FCSTD DOCUMENT  (FreeCAD 0.21R33771 (Git))
Label: EngineMount_UQM_SF_v2
License: Creative Commons Attribution-ShareAlike 4.0
LicenseURL: https://creativecommons.org/licenses/by-sa/4.0/
objects: PartDesign::CoordinateSystem×3, App::DocumentObjectGroup×3, PartDesign::Line×3, App::Link×3, Sketcher::SketchObject×2, PartDesign::Plane×2, App::Part×2, App::FeaturePython×1, PartDesign::Point×1, PartDesign::Body×1
note: 12 computed .brp shape members not serialized (recipe doc carries the construction recipe); baked Part::Feature solids carry a one-line shape summary decoded from their .brp
EXTERNAL_REF file=FacePlate_Motor_MC_v2.FCStd obj=Body_MotorFace
EXTERNAL_REF file=FacePlate_Motor_MC_v2.FCStd obj=MMFP_Tabs_CtrlMnt
EXTERNAL_REF file=FacePlate_TX_v2.FCStd obj=TXFP_SpacerSide
EXTERNAL_REF file=FacePlate_TX_v2.FCStd obj=TXFP
EXTERNAL_REF file=SpacerFlange_v2.FCStd obj=TabCenterAxis
EXTERNAL_REF file=SpacerFlange_v2.FCStd obj=TabFlange

FEATURE [PartDesign::CoordinateSystem] LCS_Origin
  AttacherType = Attacher::AttachEngine3D
  MapMode = 2
  Support = -> [X_Axis]
FEATURE [App::DocumentObjectGroup] Constraints
FEATURE [App::FeaturePython] Variables  # WARN: FeaturePython — macro-defined, semantics opaque (R4)
  Type = App::PropertyContainer
FEATURE [App::DocumentObjectGroup] Configurations
FEATURE [Sketcher::SketchObject] MotorFaceBase
  FullyConstrained = true
  MapMode = 5
  Support = -> [XY_Plane]
  expr: Constraints[1] = 16 in
  sketch-geometry (17):
    g0: Circle CenterX=0 CenterY=0 CenterZ=0 NormalX=0 NormalY=0 NormalZ=1 AngleXU=0 Radius=203.2
    g1: LineSegment StartX=-117.333 StartY=48.6008 StartZ=0 EndX=-117.333 EndY=-48.6008 EndZ=0
    g2: LineSegment StartX=-117.333 StartY=-48.6008 StartZ=0 EndX=-48.6008 EndY=-117.333 EndZ=0
    g3: LineSegment StartX=-48.6008 StartY=-117.333 StartZ=0 EndX=48.6008 EndY=-117.333 EndZ=0
    g4: LineSegment StartX=48.6008 StartY=-117.333 StartZ=0 EndX=117.333 EndY=-48.6008 EndZ=0
    g5: LineSegment StartX=117.333 StartY=-48.6008 StartZ=0 EndX=117.333 EndY=48.6008 EndZ=0
    g6: LineSegment StartX=117.333 StartY=48.6008 StartZ=0 EndX=48.6008 EndY=117.333 EndZ=0
    g7: LineSegment StartX=48.6008 StartY=117.333 StartZ=0 EndX=-48.6008 EndY=117.333 EndZ=0
    g8: LineSegment StartX=-48.6008 StartY=117.333 StartZ=0 EndX=-117.333 EndY=48.6008 EndZ=0
    g9: Circle CenterX=0 CenterY=0 CenterZ=0 NormalX=0 NormalY=0 NormalZ=1 AngleXU=0 Radius=127
    g10: LineSegment StartX=-152 StartY=0 StartZ=0 EndX=-152 EndY=17 EndZ=0
    g11: LineSegment StartX=-152 StartY=0 StartZ=0 EndX=-152 EndY=-17 EndZ=0
    g12: LineSegment StartX=-150.25 StartY=12 StartZ=0 EndX=-150.25 EndY=22 EndZ=0
    g13: LineSegment StartX=-150.25 StartY=22 StartZ=0 EndX=-153.75 EndY=22 EndZ=0
    g14: LineSegment StartX=-153.75 StartY=22 StartZ=0 EndX=-153.75 EndY=12 EndZ=0
    g15: LineSegment StartX=-153.75 StartY=12 StartZ=0 EndX=-150.25 EndY=12 EndZ=0
    g16: GeomPoint X=-152 Y=17 Z=0
  constraints (41):
    c: Coincident(g0,g-1)
    c: Diameter(g0) = 406.4
    c: Coincident(g1,g2)
    c: Coincident(g2,g3)
    c: Coincident(g3,g4)
    c: Coincident(g4,g5)
    c: Coincident(g5,g6)
    c: Coincident(g6,g7)
    c: Coincident(g7,g8)
    c: Coincident(g8,g1)
    c: Equal(g1, g2-g8) x7
    c: PointOnObject(g1,g9)
    c: PointOnObject(g2,g9)
    c: PointOnObject(g3,g9)
    c: PointOnObject(g4,g9)
    c: PointOnObject(g6,g9)
    c: PointOnObject(g7,g9)
    c: PointOnObject(g8,g9)
    c: Coincident(g9,g0)
    c: Vertical(g1)
    c: Diameter(g9) = 254
    c: PointOnObject(g5,g9)
    c: PointOnObject(g10,g-1)
    c: Vertical(g10)
    c: Coincident(g11,g10)
    c: Vertical(g11)
    c: Equal(g10,g11)
    c: DistanceY(g10,g10) = 17
    c: DistanceX(g10,g0) = 152
    c: Coincident(g12,g13)
    c: Coincident(g13,g14)
    c: Coincident(g14,g15)
    c: Coincident(g15,g12)
    c: Horizontal(g13)
    c: Horizontal(g15)
    c: Vertical(g12)
    c: Vertical(g14)
    c: Symmetric(g13,g12,g16)
    c: Coincident(g16,g10)
    c: DistanceY(g14,g14) = 10
    c: DistanceX(g13,g13) = 3.5
FEATURE [PartDesign::Line] Motor_FirstBolt
  AttacherType = Attacher::AttachEngineLine
  Length = 200
  MapMode = 46
  Placement = pos=(-117.333,48.6008,0) rot=(0,0,1;3.14159rad)
  ResizeMode = 1
  Support = -> [MotorFaceBase,XY_Plane]
FEATURE [PartDesign::Plane] MotorFace
  Length = 100
  MapMode = 5
  ResizeMode = 1
  Support = -> [XY_Plane]
  Width = 100
FEATURE [PartDesign::Line] FirstTabSlot
  AttacherType = Attacher::AttachEngineLine
  Length = 200
  MapMode = 46
  Placement = pos=(-152,17,0) rot=(0,0,1;3.14159rad)
  ResizeMode = 1
  Support = -> [MotorFaceBase,XY_Plane]
FEATURE [App::Link] MMFP_Tabs_CtrlMnt
  AttachedBy = #Body_MotorFace
  AttachedTo = Parent Assembly#MotorFace
  AttachmentOffset = pos=(0,0,0) rot=(-1,0,0;3.14159rad)
  LinkPlacement = pos=(0,0,0) rot=(-1,0,0;1.5708rad)
  LinkedObject = -> <external FacePlate_Motor_MC_v2.FCStd>#MMFP_Tabs_CtrlMnt
  Placement = pos=(0,0,0) rot=(-1,0,0;1.5708rad)
  SolverId = Asm4EE
  expr: Placement = MotorFace.Placement * AttachmentOffset * FaceFlngILC_MntTabs#Body_MotorFace.Placement ^ -1
FEATURE [Sketcher::SketchObject] MMTX_CrossSection
  FullyConstrained = true
  MapMode = 5
  Placement = pos=(0,0,0) rot=(0.57735,0.57735,0.57735;2.0944rad)
  Support = -> [YZ_Plane]
  expr: .Constraints.SpacerDepth = 38 * 2
  sketch-geometry (2):
    g0: LineSegment StartX=0 StartY=0 StartZ=0 EndX=0 EndY=3.5 EndZ=0
    g1: LineSegment StartX=0 StartY=3.5 StartZ=0 EndX=0 EndY=79.5 EndZ=0
  constraints (6):
    c: Coincident(g0,g-1)
    c: Vertical(g0)
    c: Coincident(g1,g0)
    c: Vertical(g1)
    c: DistanceY(g0,g0) = 3.5  'Thickness'
    c: DistanceY(g1,g1) = 76  'SpacerDepth'
FEATURE [PartDesign::Point] TX_CenterPoint
  AttacherType = Attacher::AttachEnginePoint
  MapMode = 37
  Placement = pos=(-1.77e-14,1.77e-14,79.5) rot=(0,0,1;0rad)
  Support = -> [MMTX_CrossSection]
FEATURE [PartDesign::Plane] TC_Face
  Length = 100
  MapMode = 6
  Placement = pos=(-1.77e-14,1.77e-14,79.5) rot=(0,0,1;3.14159rad)
  ResizeMode = 1
  Support = -> [TX_CenterPoint,XY_Plane]
  Width = 100
FEATURE [App::Link] TXFP
  AttachedBy = #TXFP_SpacerSide
  AttachedTo = Parent Assembly#TC_Face
  AttachmentOffset = pos=(0,0,0) rot=(0,-1,0;3.14159rad)
  LinkPlacement = pos=(-1.77e-14,1.77e-14,79.5) rot=(0,0,1;0rad)
  LinkedObject = -> <external FacePlate_TX_v2.FCStd>#TXFP
  Placement = pos=(-1.77e-14,1.77e-14,79.5) rot=(0,0,1;0rad)
  SolverId = Asm4EE
  expr: Placement = TC_Face.Placement * AttachmentOffset * SF_TY755_TRANS_FACEPLATE#TXFP_SpacerSide.Placement ^ -1
FEATURE [App::Link] TabFlange
  AttachedBy = #TabCenterAxis
  AttachedTo = Parent Assembly#FirstTabSlot
  AttachmentOffset = pos=(0,0,41.5) rot=(0,0,1;1.5708rad)
  LinkPlacement = pos=(-152,0,41.5) rot=(0.57735,0.57735,0.57735;4.18879rad)
  LinkedObject = -> <external SpacerFlange_v2.FCStd>#TabFlange
  Placement = pos=(-152,0,41.5) rot=(0.57735,0.57735,0.57735;4.18879rad)
  SolverId = Asm4EE
  expr: Placement = FirstTabSlot.Placement * AttachmentOffset * SpacerFlange#TabCenterAxis.Placement ^ -1
FEATURE [PartDesign::Line] CenterLine
  AttacherType = Attacher::AttachEngineLine
  Length = 200
  MapMode = 29
  ResizeMode = 1
  Support = -> [Z_Axis]
FEATURE [App::Part] Assembly
  AssemblyType = Part::Link
  Group = -> [LCS_Origin,Constraints,Variables,Configurations,MotorFaceBase,Motor_FirstBolt,MotorFace,FirstTabSlot,MMFP_Tabs_CtrlMnt,MMTX_CrossSection,TX_CenterPoint,TC_Face,TXFP,CenterLine,TabFlange]
  Origin = -> Origin
  Type = Assembly
FEATURE [PartDesign::CoordinateSystem] LCS_Origin001
  AttacherType = Attacher::AttachEngine3D
  MapMode = 2
  Support = -> [X_Axis001]
FEATURE [PartDesign::CoordinateSystem] LCS_Origin002
  AttacherType = Attacher::AttachEngine3D
  MapMode = 2
  Support = -> [X_Axis002]
FEATURE [PartDesign::Body] Body
  Group = -> [LCS_Origin002]
  Origin = -> Origin002
FEATURE [App::Part] TabFlangePattern
  Group = -> [LCS_Origin001,Body]
  Origin = -> Origin001
FEATURE [App::DocumentObjectGroup] Parts
  Group = -> [TabFlangePattern]

RESOLVED EXTERNAL PARTS (link-assembly join: the EXTERNAL_REF files above that resolve inside this repo's crawl, each included once):
---- part FacePlate_Motor_MC_v2.FCStd = doc fcstd_9c76934eff34 ----
FCSTD DOCUMENT  (FreeCAD 0.21R33771 (Git))
Label: FacePlate_Motor_MC_v2
License: Creative Commons Attribution-ShareAlike 4.0
LicenseURL: https://creativecommons.org/licenses/by-sa/4.0/
objects: Sketcher::SketchObject×5, PartDesign::Line×4, PartDesign::Pocket×3, PartDesign::Pad×2, PartDesign::PolarPattern×2, PartDesign::Plane×2, PartDesign::CoordinateSystem×1, PartDesign::Fillet×1, PartDesign::Body×1, App::Part×1
note: 27 computed .brp shape members not serialized (recipe doc carries the construction recipe); baked Part::Feature solids carry a one-line shape summary decoded from their .brp

FEATURE [Sketcher::SketchObject] Sketch
  FullyConstrained = true
  MapMode = 5
  Placement = pos=(0,0,0) rot=(1,0,0;1.5708rad)
  Support = -> [XZ_Plane]
  sketch-geometry (24):
    g0: Circle CenterX=0 CenterY=0 CenterZ=0 NormalX=0 NormalY=0 NormalZ=1 AngleXU=0 Radius=127
    g1: Circle CenterX=-127 CenterY=0 CenterZ=0 NormalX=0 NormalY=0 NormalZ=1 AngleXU=0 Radius=15
    g2: LineSegment StartX=-127 StartY=0 StartZ=0 EndX=-142 EndY=0 EndZ=0
    g3: Circle CenterX=0 CenterY=0 CenterZ=0 NormalX=0 NormalY=0 NormalZ=1 AngleXU=0 Radius=200
    g4: Circle CenterX=0 CenterY=0 CenterZ=0 NormalX=0 NormalY=0 NormalZ=1 AngleXU=0 Radius=100
    g5: LineSegment StartX=-152 StartY=62.9605 StartZ=0 EndX=-152 EndY=-62.9605 EndZ=0
    g6: LineSegment StartX=-152 StartY=-62.9605 StartZ=0 EndX=-62.9605 EndY=-152 EndZ=0
    g7: LineSegment StartX=-62.9605 StartY=-152 StartZ=0 EndX=62.9605 EndY=-152 EndZ=0
    g8: LineSegment StartX=62.9605 StartY=-152 StartZ=0 EndX=152 EndY=-62.9605 EndZ=0
    g9: LineSegment StartX=152 StartY=-62.9605 StartZ=0 EndX=152 EndY=62.9605 EndZ=0
    g10: LineSegment StartX=152 StartY=62.9605 StartZ=0 EndX=62.9605 EndY=152 EndZ=0
    g11: LineSegment StartX=62.9605 StartY=152 StartZ=0 EndX=-62.9605 EndY=152 EndZ=0
    g12: LineSegment StartX=-62.9605 StartY=152 StartZ=0 EndX=-152 EndY=62.9605 EndZ=0
    g13: Circle CenterX=0 CenterY=0 CenterZ=0 NormalX=0 NormalY=0 NormalZ=1 AngleXU=0 Radius=164.524
    g14: LineSegment StartX=-153.75 StartY=22.75 StartZ=0 EndX=-153.75 EndY=33.25 EndZ=0
    g15: LineSegment StartX=-153.75 StartY=33.25 StartZ=0 EndX=-150.25 EndY=33.25 EndZ=0
    g16: LineSegment StartX=-150.25 StartY=33.25 StartZ=0 EndX=-150.25 EndY=22.75 EndZ=0
    g17: LineSegment StartX=-150.25 StartY=22.75 StartZ=0 EndX=-153.75 EndY=22.75 EndZ=0
    g18: GeomPoint X=-152 Y=28 Z=0
    g19: LineSegment StartX=-150.25 StartY=-22.75 StartZ=0 EndX=-150.25 EndY=-33.25 EndZ=0
    g20: LineSegment StartX=-150.25 StartY=-33.25 StartZ=0 EndX=-153.75 EndY=-33.25 EndZ=0
    g21: LineSegment StartX=-153.75 StartY=-33.25 StartZ=0 EndX=-153.75 EndY=-22.75 EndZ=0
    g22: LineSegment StartX=-153.75 StartY=-22.75 StartZ=0 EndX=-150.25 EndY=-22.75 EndZ=0
    g23: GeomPoint X=-152 Y=-28 Z=0
  constraints (60):
    c: Coincident(g0,g-1)
    c: PointOnObject(g1,g0)
    c: Diameter(g1) = 30
    c: Diameter(g0) = 254
    c: PointOnObject(g1,g-1)
    c: Coincident(g2,g1)
    c: PointOnObject(g2,g1)
    c: Horizontal(g2)
    c: Coincident(g3,g0)
    c: Diameter(g3) = 400
    c: Diameter(g4) = 200
    c: Coincident(g4,g3)
    c: Coincident(g5,g6)
    c: Coincident(g6,g7)
    c: Coincident(g7,g8)
    c: Coincident(g8,g9)
    c: Coincident(g9,g10)
    c: Coincident(g10,g11)
    c: Coincident(g11,g12)
    c: Coincident(g12,g5)
    c: Equal(g5, g6-g12) x7
    c: PointOnObject(g5,g13)
    c: PointOnObject(g6,g13)
    c: PointOnObject(g7,g13)
    c: PointOnObject(g8,g13)
    c: PointOnObject(g9,g13)
    c: PointOnObject(g10,g13)
    c: PointOnObject(g11,g13)
    c: PointOnObject(g12,g13)
    c: Coincident(g13,g3)
    c: Vertical(g5)
    c: DistanceX(g5,g2) = 10
    c: Coincident(g14,g15)
    c: Coincident(g15,g16)
    c: Coincident(g16,g17)
    c: Coincident(g17,g14)
    c: Horizontal(g15)
    c: Horizontal(g17)
    c: Vertical(g14)
    c: Vertical(g16)
    c: Symmetric(g15,g14,g18)
    c: PointOnObject(g18,g5)
    c: Coincident(g19,g20)
    c: Coincident(g20,g21)
    c: Coincident(g21,g22)
    c: Coincident(g22,g19)
    c: Horizontal(g20)
    c: Horizontal(g22)
    c: Vertical(g19)
    c: Vertical(g21)
    c: Symmetric(g20,g19,g23)
    c: PointOnObject(g23,g5)
    c: Equal(g14,g21)
    c: Equal(g15,g22)
    c: DistanceX(g15,g15) = 3.5
    c: DistanceY(g14,g14) = 10.5
    c: DistanceY(g3,g14) = 22.75
    c: DistanceY(g19,g3) = 22.75
    c: DistanceY(g3,g18) = 28
    c: DistanceY(g23,g3) = 28
FEATURE [PartDesign::Pad] Pad
  Direction = (0,-1,-2e-16)
  Length = 3
  Length2 = 10
  Placement = pos=(0,0,0) rot=(1,0,0;1.5708rad)
  Profile = -> Sketch
  ReferenceAxis = -> Sketch [N_Axis]
  Type = 0
FEATURE [Sketcher::SketchObject] Sketch001
  FullyConstrained = true
  MapMode = 5
  Placement = pos=(0,0,0) rot=(1,0,0;1.5708rad)
  Support = -> [XZ_Plane]
  expr: Constraints[10] = Sketch.Constraints[10]
  expr: Constraints[2] = Sketch.Constraints[2]
  expr: Constraints[37] = Sketch.Constraints[37]
  expr: Constraints[3] = Sketch.Constraints[3]
  expr: Constraints[61] = Sketch.Constraints[61]
  expr: Constraints[9] = Sketch.Constraints[9]
  sketch-geometry (24):
    g0: Circle CenterX=0 CenterY=0 CenterZ=0 NormalX=0 NormalY=0 NormalZ=1 AngleXU=0 Radius=127
    g1: Circle CenterX=-127 CenterY=0 CenterZ=0 NormalX=0 NormalY=0 NormalZ=1 AngleXU=0 Radius=15
    g2: LineSegment StartX=-127 StartY=0 StartZ=0 EndX=-142 EndY=0 EndZ=0
    g3: Circle CenterX=0 CenterY=0 CenterZ=0 NormalX=0 NormalY=0 NormalZ=1 AngleXU=0 Radius=200
    g4: Circle CenterX=0 CenterY=0 CenterZ=0 NormalX=0 NormalY=0 NormalZ=1 AngleXU=0 Radius=100
    g5: LineSegment StartX=-152 StartY=62.9605 StartZ=0 EndX=-152 EndY=-62.9605 EndZ=0
    g6: LineSegment StartX=-152 StartY=-62.9605 StartZ=0 EndX=-62.9605 EndY=-152 EndZ=0
    g7: LineSegment StartX=-62.9605 StartY=-152 StartZ=0 EndX=62.9605 EndY=-152 EndZ=0
    g8: LineSegment StartX=62.9605 StartY=-152 StartZ=0 EndX=152 EndY=-62.9605 EndZ=0
    g9: LineSegment StartX=152 StartY=-62.9605 StartZ=0 EndX=152 EndY=62.9605 EndZ=0
    g10: LineSegment StartX=152 StartY=62.9605 StartZ=0 EndX=62.9605 EndY=152 EndZ=0
    g11: LineSegment StartX=62.9605 StartY=152 StartZ=0 EndX=-62.9605 EndY=152 EndZ=0
    g12: LineSegment StartX=-62.9605 StartY=152 StartZ=0 EndX=-152 EndY=62.9605 EndZ=0
    g13: Circle CenterX=0 CenterY=0 CenterZ=0 NormalX=0 NormalY=0 NormalZ=1 AngleXU=0 Radius=164.524
    g14: LineSegment StartX=-153.75 StartY=22.75 StartZ=0 EndX=-153.75 EndY=33.25 EndZ=0
    g15: LineSegment StartX=-153.75 StartY=33.25 StartZ=0 EndX=-150.25 EndY=33.25 EndZ=0
    g16: LineSegment StartX=-150.25 StartY=33.25 StartZ=0 EndX=-150.25 EndY=22.75 EndZ=0
    g17: LineSegment StartX=-150.25 StartY=22.75 StartZ=0 EndX=-153.75 EndY=22.75 EndZ=0
    g18: GeomPoint X=-152 Y=28 Z=0
    g19: LineSegment StartX=-150.25 StartY=-22.75 StartZ=0 EndX=-150.25 EndY=-33.25 EndZ=0
    g20: LineSegment StartX=-150.25 StartY=-33.25 StartZ=0 EndX=-153.75 EndY=-33.25 EndZ=0
    g21: LineSegment StartX=-153.75 StartY=-33.25 StartZ=0 EndX=-153.75 EndY=-22.75 EndZ=0
    g22: LineSegment StartX=-153.75 StartY=-22.75 StartZ=0 EndX=-150.25 EndY=-22.75 EndZ=0
    g23: GeomPoint X=-152 Y=-28 Z=0
  constraints (62):
    c: Coincident(g0,g-1)
    c: PointOnObject(g1,g0)
    c: Diameter(g1) = 30
    c: Diameter(g0) = 254
    c: PointOnObject(g1,g-1)
    c: Coincident(g2,g1)
    c: PointOnObject(g2,g1)
    c: Horizontal(g2)
    c: Coincident(g3,g0)
    c: Diameter(g3) = 400
    c: Diameter(g4) = 200
    c: Coincident(g4,g3)
    c: Coincident(g5,g6)
    c: Coincident(g6,g7)
    c: Coincident(g7,g8)
    c: Coincident(g8,g9)
    c: Coincident(g9,g10)
    c: Coincident(g10,g11)
    c: Coincident(g11,g12)
    c: Coincident(g12,g5)
    c: Equal(g5, g6-g12) x7
    c: PointOnObject(g5,g13)
    c: PointOnObject(g6,g13)
    c: PointOnObject(g7,g13)
    c: PointOnObject(g8,g13)
    c: PointOnObject(g9,g13)
    c: PointOnObject(g10,g13)
    c: PointOnObject(g11,g13)
    c: PointOnObject(g12,g13)
    c: Coincident(g13,g3)
    c: Vertical(g5)
    c: DistanceX(g5,g2) = 10
    c: Coincident(g14,g15)
    c: Coincident(g15,g16)
    c: Coincident(g16,g17)
    c: Coincident(g17,g14)
    c: Horizontal(g15)
    c: Horizontal(g17)
    c: Vertical(g14)
    c: Vertical(g16)
    c: Symmetric(g15,g14,g18)
    c: PointOnObject(g18,g5)
    c: Coincident(g19,g20)
    c: Coincident(g20,g21)
    c: Coincident(g21,g22)
    c: Coincident(g22,g19)
    c: Horizontal(g20)
    c: Horizontal(g22)
    c: Vertical(g19)
    c: Vertical(g21)
    c: Symmetric(g20,g19,g23)
    c: PointOnObject(g23,g5)
    c: Equal(g14,g21)
    c: Equal(g15,g22)
    c: DistanceX(g15,g15) = 3.5
    c: DistanceY(g14,g14) = 10.5
    c: DistanceY(g3,g14) = 22.75
    c: DistanceY(g19,g3) = 22.75
    c: DistanceX(g18,g0) = 152
    c: DistanceY(g0,g5) = 62.9605
    c: DistanceY(g0,g18) = 28
    c: DistanceY(g23,g0) = 28
FEATURE [PartDesign::Pocket] Pocket
  BaseFeature = -> Pad
  Direction = (0,1,2e-16)
  Length = 5
  Length2 = 5
  Placement = pos=(0,0,0) rot=(1,0,0;1.5708rad)
  Profile = -> Sketch001
  ReferenceAxis = -> Sketch001 [N_Axis]
  Reversed = true
  Type = 1
FEATURE [PartDesign::PolarPattern] PolarPattern
  Angle = 360
  Axis = -> Sketch001 [N_Axis]
  BaseFeature = -> Pocket
  Occurrences = 8
  Originals = -> [Pocket]
  Placement = pos=(0,0,0) rot=(1,0,0;1.5708rad)
FEATURE [Sketcher::SketchObject] Sketch002
  FullyConstrained = true
  MapMode = 5
  Placement = pos=(0,0,0) rot=(1,0,0;1.5708rad)
  Support = -> [XZ_Plane]
  sketch-geometry (17):
    g0: LineSegment StartX=117.333 StartY=48.6008 StartZ=0 EndX=48.6008 EndY=117.333 EndZ=0
    g1: LineSegment StartX=48.6008 StartY=117.333 StartZ=0 EndX=-48.6008 EndY=117.333 EndZ=0
    g2: LineSegment StartX=-48.6008 StartY=117.333 StartZ=0 EndX=-117.333 EndY=48.6008 EndZ=0
    g3: LineSegment StartX=-117.333 StartY=48.6008 StartZ=0 EndX=-117.333 EndY=-48.6008 EndZ=0
    g4: LineSegment StartX=-117.333 StartY=-48.6008 StartZ=0 EndX=-48.6008 EndY=-117.333 EndZ=0
    g5: LineSegment StartX=-48.6008 StartY=-117.333 StartZ=0 EndX=48.6008 EndY=-117.333 EndZ=0
    g6: LineSegment StartX=48.6008 StartY=-117.333 StartZ=0 EndX=117.333 EndY=-48.6008 EndZ=0
    g7: LineSegment StartX=117.333 StartY=-48.6008 StartZ=0 EndX=117.333 EndY=48.6008 EndZ=0
    g8: Circle CenterX=0 CenterY=0 CenterZ=0 NormalX=0 NormalY=0 NormalZ=1 AngleXU=0 Radius=127
    g9: Circle CenterX=-117.333 CenterY=48.6008 CenterZ=0 NormalX=0 NormalY=0 NormalZ=1 AngleXU=0 Radius=5
    g10: Circle CenterX=-48.6008 CenterY=117.333 CenterZ=0 NormalX=0 NormalY=0 NormalZ=1 AngleXU=0 Radius=5
    g11: Circle CenterX=48.6008 CenterY=117.333 CenterZ=0 NormalX=0 NormalY=0 NormalZ=1 AngleXU=0 Radius=5
    g12: Circle CenterX=117.333 CenterY=48.6008 CenterZ=0 NormalX=0 NormalY=0 NormalZ=1 AngleXU=0 Radius=5
    g13: Circle CenterX=117.333 CenterY=-48.6008 CenterZ=0 NormalX=0 NormalY=0 NormalZ=1 AngleXU=0 Radius=5
    g14: Circle CenterX=48.6008 CenterY=-117.333 CenterZ=0 NormalX=0 NormalY=0 NormalZ=1 AngleXU=0 Radius=5
    g15: Circle CenterX=-48.6008 CenterY=-117.333 CenterZ=0 NormalX=0 NormalY=0 NormalZ=1 AngleXU=0 Radius=5
    g16: Circle CenterX=-117.333 CenterY=-48.6008 CenterZ=0 NormalX=0 NormalY=0 NormalZ=1 AngleXU=0 Radius=5
  constraints (36):
    c: Coincident(g0,g1)
    c: Coincident(g1,g2)
    c: Coincident(g2,g3)
    c: Coincident(g3,g4)
    c: Coincident(g4,g5)
    c: Coincident(g5,g6)
    c: Coincident(g6,g7)
    c: Coincident(g7,g0)
    c: Equal(g0, g1-g7) x7
    c: PointOnObject(g0,g8)
    c: PointOnObject(g1,g8)
    c: PointOnObject(g2,g8)
    c: PointOnObject(g3,g8)
    c: PointOnObject(g4,g8)
    c: PointOnObject(g5,g8)
    c: PointOnObject(g6,g8)
    c: PointOnObject(g7,g8)
    c: Coincident(g8,g-1)
    c: Diameter(g8) = 254
    c: Vertical(g3)
    c: Coincident(g9,g2)
    c: Coincident(g10,g1)
    c: Coincident(g11,g0)
    c: Coincident(g12,g0)
    c: Coincident(g13,g6)
    c: Coincident(g14,g5)
    c: Coincident(g15,g4)
    c: Coincident(g16,g3)
    c: Equal(g9,g10)
    c: Equal(g10,g11)
    c: Equal(g11,g12)
    c: Equal(g12,g13)
    c: Equal(g13,g14)
    c: Equal(g14,g15)
    c: Equal(g15,g16)
    c: Diameter(g9) = 10
FEATURE [PartDesign::Pocket] Pocket001
  BaseFeature = -> PolarPattern
  Direction = (0,1,2e-16)
  Length = 5
  Length2 = 5
  Placement = pos=(0,0,0) rot=(1,0,0;1.5708rad)
  Profile = -> Sketch002
  ReferenceAxis = -> Sketch002 [N_Axis]
  Reversed = true
  Type = 0
FEATURE [Sketcher::SketchObject] Sketch003
  FullyConstrained = false
  MapMode = 5
  Placement = pos=(0,0,0) rot=(1,0,0;1.5708rad)
  Support = -> [XZ_Plane]
  sketch-geometry (24):
    g0: LineSegment StartX=0 StartY=0 StartZ=0 EndX=0 EndY=203 EndZ=0
    g1: LineSegment StartX=-197.594 StartY=203 StartZ=0 EndX=0 EndY=203 EndZ=0
    g2: LineSegment StartX=0 StartY=203 StartZ=0 EndX=197.594 EndY=203 EndZ=0
    g3: Circle CenterX=-100 CenterY=189.5 CenterZ=0 NormalX=0 NormalY=0 NormalZ=1 AngleXU=0 Radius=4.5
    g4: Circle CenterX=-140 CenterY=189.5 CenterZ=0 NormalX=0 NormalY=0 NormalZ=1 AngleXU=0 Radius=4.5
    g5: Circle CenterX=100 CenterY=189.5 CenterZ=0 NormalX=0 NormalY=0 NormalZ=1 AngleXU=0 Radius=4.5
    g6: Circle CenterX=140 CenterY=189.5 CenterZ=0 NormalX=0 NormalY=0 NormalZ=1 AngleXU=0 Radius=4.5
    g7: LineSegment StartX=-197.594 StartY=203 StartZ=0 EndX=-197.594 EndY=2.84e-14 EndZ=0
    g8: LineSegment StartX=-140 StartY=189.5 StartZ=0 EndX=-100 EndY=189.5 EndZ=0
    g9: LineSegment StartX=-100 StartY=189.5 StartZ=0 EndX=0 EndY=189.5 EndZ=0
    g10: LineSegment StartX=0 StartY=189.5 StartZ=0 EndX=100 EndY=189.5 EndZ=0
    g11: LineSegment StartX=100 StartY=189.5 StartZ=0 EndX=140 EndY=189.5 EndZ=0
    g12: LineSegment StartX=197.594 StartY=203 StartZ=0 EndX=197.594 EndY=0 EndZ=0
    g13: Circle CenterX=-162.827 CenterY=167.281 CenterZ=0 NormalX=0 NormalY=0 NormalZ=1 AngleXU=0 Radius=12.5
    g14: Circle CenterX=162.827 CenterY=167.281 CenterZ=0 NormalX=0 NormalY=0 NormalZ=1 AngleXU=0 Radius=12.5
    g15: LineSegment StartX=0 StartY=0 StartZ=0 EndX=-162.827 EndY=167.281 EndZ=0
    g16: LineSegment StartX=-162.827 StartY=167.281 StartZ=0 EndX=-197.594 EndY=203 EndZ=0
    g17: LineSegment StartX=0 StartY=0 StartZ=0 EndX=162.827 EndY=167.281 EndZ=0
    g18: LineSegment StartX=162.827 StartY=167.281 StartZ=0 EndX=197.594 EndY=203 EndZ=0
    g19: LineSegment StartX=-140 StartY=189.5 StartZ=0 EndX=-126.131 EndY=203 EndZ=0
    g20: LineSegment StartX=-162.827 StartY=167.281 StartZ=0 EndX=-153.869 EndY=176 EndZ=0
    g21: LineSegment StartX=-153.869 StartY=176 StartZ=0 EndX=-140 EndY=189.5 EndZ=0
    g22: LineSegment StartX=-140 StartY=189.5 StartZ=0 EndX=-140 EndY=194 EndZ=0
    g23: ArcOfCircle CenterX=0 CenterY=0 CenterZ=0 NormalX=0 NormalY=0 NormalZ=1 AngleXU=0 Radius=197.594 StartAngle=0 EndAngle=3.14159
  constraints (63):
    c: Coincident(g0,g-1)
    c: Vertical(g0)
    c: DistanceY(g0,g0) = 203
    c: Coincident(g1,g0)
    c: Horizontal(g1)
    c: Coincident(g2,g1)
    c: Horizontal(g2)
    c: Coincident(g7,g1)
    c: PointOnObject(g7,g-1)
    c: Vertical(g7)
    c: Diameter(g3) = 9
    c: Equal(g3,g4)
    c: Equal(g3,g5)
    c: Equal(g5,g6)
    c: Coincident(g8,g4)
    c: Coincident(g8,g3)
    c: Horizontal(g8)
    c: Coincident(g9,g3)
    c: PointOnObject(g9,g0)
    c: Horizontal(g9)
    c: Coincident(g10,g9)
    c: Coincident(g10,g5)
    c: Horizontal(g10)
    c: Coincident(g11,g5)
    c: Coincident(g11,g6)
    c: Horizontal(g11)
    c: Coincident(g12,g2)
    c: PointOnObject(g12,g-1)
    c: Vertical(g12)
    c: Diameter(g13) = 25
    c: Coincident(g15,g0)
    c: Coincident(g15,g13)
    c: Coincident(g16,g13)
    c: Coincident(g16,g1)
    c: Parallel(g16,g15)
    c: Coincident(g17,g0)
    c: Coincident(g17,g14)
    c: Coincident(g18,g14)
    c: Coincident(g18,g2)
    c: Parallel(g18,g17)
    c: Equal(g15,g17)
    c: Equal(g8,g11)
    c: Equal(g9,g10)
    c: DistanceX(g8,g8) = 40
    c: DistanceX(g9,g9) = 100
    c: Equal(g1,g2)
    c: Coincident(g20,g13)
    c: Coincident(g21,g4)
    c: Coincident(g19,g4)
    c: PointOnObject(g19,g1)
    c: Coincident(g20,g21)
    c: Perpendicular(g15,g20)
    c: Perpendicular(g15,g21)
    c: Parallel(g19,g20)
    c: PointOnObject(g20,g13)
    c: Equal(g21,g19)
    c: Coincident(g22,g4)
    c: PointOnObject(g22,g4)
    c: Vertical(g22)
    c: DistanceY(g22,g1) = 9
    c: Equal(g14,g13)
    c: Coincident(g23,g0)
    c: Coincident(g23,g7)
FEATURE [PartDesign::Pad] Pad001
  BaseFeature = -> Pocket001
  Direction = (0,-1,-2e-16)
  Length = 3
  Length2 = 10
  Placement = pos=(0,0,0) rot=(1,0,0;1.5708rad)
  Profile = -> Sketch003
  ReferenceAxis = -> Sketch003 [N_Axis]
  Type = 0
FEATURE [PartDesign::CoordinateSystem] LCS_Origin
  AttacherType = Attacher::AttachEngine3D
  MapMode = 2
  Support = -> [X_Axis001]
FEATURE [PartDesign::Line] MM_FirstBolt
  AttacherType = Attacher::AttachEngineLine
  Length = 200
  MapMode = 19
  Placement = pos=(-117.333,-1.08e-14,48.6008) rot=(1,0,0;1.5708rad)
  ResizeMode = 1
  Support = -> [Sketch002]
FEATURE [PartDesign::Plane] MotorFace
  Length = 100
  MapMode = 5
  Placement = pos=(0,0,0) rot=(-1,0,0;1.5708rad)
  ResizeMode = 1
  Support = -> [Pad001]
  Width = 100
FEATURE [PartDesign::Line] MotorCenterline
  AttacherType = Attacher::AttachEngineLine
  Length = 200
  MapMode = 42
  Placement = pos=(4.752e-13,0,3.4e-15) rot=(0,0.707107,0.707107;3.14159rad)
  ResizeMode = 1
  Support = -> [Sketch]
FEATURE [PartDesign::Line] Body_MotorCenterline
  AttachedBy = Origin
  AttacherType = Attacher::AttachEngineLine
  Length = 200
  Placement = pos=(4.75e-13,0,3e-15) rot=(0,0.707107,0.707107;3.14159rad)
  ResizeMode = 1
  SolverId = Asm4EE
  expr: Placement = Body.Placement * MotorCenterline.Placement
FEATURE [PartDesign::Plane] Body_MotorFace
  AttachedBy = Origin
  Length = 100
  Placement = pos=(0,0,0) rot=(-1,0,0;1.5708rad)
  ResizeMode = 1
  SolverId = Asm4EE
  Width = 100
  expr: Placement = Body.Placement * MotorFace.Placement
FEATURE [PartDesign::Line] Body_MM_FirstBolt
  AttachedBy = Origin
  AttacherType = Attacher::AttachEngineLine
  Length = 200
  Placement = pos=(-117.333,-1.1e-14,48.6008) rot=(1,0,0;1.5708rad)
  ResizeMode = 1
  SolverId = Asm4EE
  expr: Placement = Body.Placement * MM_FirstBolt.Placement
FEATURE [Sketcher::SketchObject] Sketch004
  FullyConstrained = true
  MapMode = 5
  Placement = pos=(0,0,0) rot=(1,0,0;1.5708rad)
  Support = -> [XZ_Plane]
  sketch-geometry (5):
    g0: LineSegment StartX=-174.75 StartY=-1.75 StartZ=0 EndX=-174.75 EndY=1.75 EndZ=0
    g1: LineSegment StartX=-174.75 StartY=1.75 StartZ=0 EndX=-185.25 EndY=1.75 EndZ=0
    g2: LineSegment StartX=-185.25 StartY=1.75 StartZ=0 EndX=-185.25 EndY=-1.75 EndZ=0
    g3: LineSegment StartX=-185.25 StartY=-1.75 StartZ=0 EndX=-174.75 EndY=-1.75 EndZ=0
    g4: GeomPoint X=-180 Y=0 Z=0
  constraints (14):
    c: Coincident(g0,g1)
    c: Coincident(g1,g2)
    c: Coincident(g2,g3)
    c: Coincident(g3,g0)
    c: Horizontal(g1)
    c: Horizontal(g3)
    c: Vertical(g0)
    c: Vertical(g2)
    c: Symmetric(g1,g0,g4)
    c: PointOnObject(g4,g-1)
    c: DistanceY(g2,g2) = 3.5
    c: DistanceX(g1,g1) = 10.5
    c: DistanceX(g2,g-1) = 185.25
    c: DistanceX(g4,g-1) = 180
FEATURE [PartDesign::Pocket] Pocket002
  BaseFeature = -> Pad001
  Direction = (0,1,2e-16)
  Length = 5
  Length2 = 5
  Midplane = true
  Placement = pos=(0,0,0) rot=(1,0,0;1.5708rad)
  Profile = -> Sketch004
  ReferenceAxis = -> Sketch004 [N_Axis]
  Type = 1
FEATURE [PartDesign::PolarPattern] PolarPattern001
  Angle = 360
  Axis = -> Y_Axis
  BaseFeature = -> Pocket002
  Occurrences = 8
  Originals = -> [Pocket002]
  Placement = pos=(0,0,0) rot=(1,0,0;1.5708rad)
FEATURE [PartDesign::Fillet] Fillet
  Base = -> PolarPattern001 [Edge377,Edge124]
  BaseFeature = -> PolarPattern001
  Placement = pos=(0,0,0) rot=(1,0,0;1.5708rad)
  Radius = 50
  SupportTransform = false
  UseAllEdges = false
FEATURE [PartDesign::Body] Body  label="MotorMount_CtrlMnt"
  Group = -> [Sketch,Pad,Sketch001,Pocket,PolarPattern,Sketch002,Pocket001,Sketch003,Pad001,MM_FirstBolt,MotorFace,MotorCenterline,Sketch004,Pocket002,PolarPattern001,Fillet]
  Origin = -> Origin
  Tip = -> Fillet
FEATURE [App::Part] MMFP_Tabs_CtrlMnt
  Group = -> [LCS_Origin,Body,Body_MotorCenterline,Body_MotorFace,Body_MM_FirstBolt]
  Origin = -> Origin001
---- part FacePlate_TX_v2.FCStd = doc fcstd_3f7f41f5f805 ----
FCSTD DOCUMENT  (FreeCAD 0.21R33771 (Git))
Label: FacePlate_TX_v2
License: All rights reserved
LicenseURL: http://en.wikipedia.org/wiki/All_rights_reserved
objects: Sketcher::SketchObject×6, PartDesign::Pocket×3, PartDesign::PolarPattern×3, PartDesign::CoordinateSystem×2, Part::Feature×1, PartDesign::Pad×1, PartDesign::Plane×1, PartDesign::Line×1, PartDesign::Body×1, App::Part×1
note: 23 computed .brp shape members not serialized (recipe doc carries the construction recipe); baked Part::Feature solids carry a one-line shape summary decoded from their .brp

FEATURE [Part::Feature] Part__Feature126  label="plate33"
  shape: bbox 408 x 387 x 80.02 mm, 236 faces, 3 solids (baked)
FEATURE [Sketcher::SketchObject] Sketch  label="IMPORTED_BP"
  FullyConstrained = true
  MapMode = 2
  Support = -> [XY_Plane]
  sketch-geometry (10):
    g0: Circle CenterX=-137.568 CenterY=110.686 CenterZ=0 NormalX=0 NormalY=0 NormalZ=1 AngleXU=0 Radius=5.75
    g1: Circle CenterX=-170.744 CenterY=68.6485 CenterZ=0 NormalX=0 NormalY=0 NormalZ=1 AngleXU=0 Radius=5.75
    g2: Circle CenterX=-179.453 CenterY=19.5185 CenterZ=0 NormalX=0 NormalY=0 NormalZ=1 AngleXU=0 Radius=5.75
    g3: Circle CenterX=-171.59 CenterY=-42.6229 CenterZ=0 NormalX=0 NormalY=0 NormalZ=1 AngleXU=0 Radius=5.75
    g4: Circle CenterX=-105.528 CenterY=-141.847 CenterZ=0 NormalX=0 NormalY=0 NormalZ=1 AngleXU=0 Radius=5.75
    g5: Circle CenterX=107.083 CenterY=-141.845 CenterZ=0 NormalX=0 NormalY=0 NormalZ=1 AngleXU=0 Radius=5.75
    g6: Circle CenterX=162.173 CenterY=-89.3634 CenterZ=0 NormalX=0 NormalY=0 NormalZ=1 AngleXU=0 Radius=5.75
    g7: Circle CenterX=176.51 CenterY=-18.0151 CenterZ=0 NormalX=0 NormalY=0 NormalZ=1 AngleXU=0 Radius=5.75
    g8: Circle CenterX=163.102 CenterY=62.0411 CenterZ=0 NormalX=0 NormalY=0 NormalZ=1 AngleXU=0 Radius=5.75
    g9: Circle CenterX=128.64 CenterY=110.662 CenterZ=0 NormalX=0 NormalY=0 NormalZ=1 AngleXU=0 Radius=5.75
  constraints (20):
    c: Diameter(g0) = 11.5
    c: Equal(g0,g1)
    c: Equal(g1,g2)
    c: Equal(g2,g3)
    c: Equal(g3,g4)
    c: Equal(g4,g5)
    c: Equal(g5,g6)
    c: Equal(g6,g7)
    c: Equal(g7,g8)
    c: Equal(g8,g9)
    c: Block(g6)
    c: Block(g0)
    c: Block(g1)
    c: Block(g2)
    c: Block(g3)
    c: Block(g4)
    c: Block(g5)
    c: Block(g7)
    c: Block(g8)
    c: Block(g9)
FEATURE [Sketcher::SketchObject] Sketch001  label="SF_Trans_BP"
  FullyConstrained = false
  MapMode = 5
  Support = -> [XY_Plane]
  expr: Constraints[2] = 16 in
  expr: Constraints[33] = 3.5 * 3.5
  expr: Constraints[9] = Sketch.Constraints[0]
  sketch-geometry (16):
    g0: Circle CenterX=0 CenterY=0 CenterZ=0 NormalX=0 NormalY=0 NormalZ=1 AngleXU=0 Radius=127
    g1: Circle CenterX=0 CenterY=0 CenterZ=0 NormalX=0 NormalY=0 NormalZ=1 AngleXU=0 Radius=203.2
    g2: Circle CenterX=0 CenterY=0 CenterZ=0 NormalX=0 NormalY=0 NormalZ=1 AngleXU=0 Radius=139.75
    g3: LineSegment StartX=-203.2 StartY=0 StartZ=0 EndX=-148.2 EndY=0 EndZ=0
    g4: LineSegment StartX=-148.2 StartY=0 StartZ=0 EndX=-139.75 EndY=0 EndZ=0
    g5: Circle CenterX=-137.568 CenterY=110.686 CenterZ=0 NormalX=0 NormalY=0 NormalZ=1 AngleXU=0 Radius=5.75
    g6: Circle CenterX=-170.744 CenterY=68.6485 CenterZ=0 NormalX=0 NormalY=0 NormalZ=1 AngleXU=0 Radius=5.75
    g7: Circle CenterX=-179.453 CenterY=19.5185 CenterZ=0 NormalX=0 NormalY=0 NormalZ=1 AngleXU=0 Radius=5.75
    g8: Circle CenterX=-171.59 CenterY=-42.6229 CenterZ=0 NormalX=0 NormalY=0 NormalZ=1 AngleXU=0 Radius=5.75
    g9: Circle CenterX=-105.528 CenterY=-141.847 CenterZ=0 NormalX=0 NormalY=0 NormalZ=1 AngleXU=0 Radius=5.75
    g10: Circle CenterX=107.083 CenterY=-141.845 CenterZ=0 NormalX=0 NormalY=0 NormalZ=1 AngleXU=0 Radius=5.75
    g11: Circle CenterX=162.173 CenterY=-89.3634 CenterZ=0 NormalX=0 NormalY=0 NormalZ=1 AngleXU=0 Radius=5.75
    g12: Circle CenterX=176.51 CenterY=-18.0151 CenterZ=0 NormalX=0 NormalY=0 NormalZ=1 AngleXU=0 Radius=5.75
    g13: Circle CenterX=163.102 CenterY=62.0411 CenterZ=0 NormalX=0 NormalY=0 NormalZ=1 AngleXU=0 Radius=5.75
    g14: Circle CenterX=128.64 CenterY=110.662 CenterZ=0 NormalX=0 NormalY=0 NormalZ=1 AngleXU=0 Radius=5.75
    g15: GeomPoint X=-152 Y=0 Z=0
  constraints (34):
    c: Coincident(g0,g-1)
    c: Diameter(g0) = 254
    c: Diameter(g1) = 406.4
    c: Coincident(g1,g0)
    c: PointOnObject(g3,g1)
    c: PointOnObject(g3,g-1)
    c: DistanceX(g3,g3) = 55
    c: Coincident(g4,g3)
    c: Horizontal(g4)
    c: Diameter(g5) = 11.5
    c: Equal(g5,g6)
    c: Equal(g6,g7)
    c: Equal(g7,g8)
    c: Equal(g8,g9)
    c: Equal(g9,g10)
    c: Equal(g10,g11)
    c: Equal(g11,g12)
    c: Equal(g12,g13)
    c: Equal(g13,g14)
    c: Block(g11)
    c: Block(g5)
    c: Block(g6)
    c: Block(g7)
    c: Block(g8)
    c: Block(g9)
    c: Block(g10)
    c: Block(g12)
    c: Block(g13)
    c: Block(g14)
    c: DistanceX(g15,g1) = 152  'TabRadialPos'
    c: PointOnObject(g4,g2)
    c: PointOnObject(g3,g-1)
    c: Coincident(g2,g1)
    c: DistanceX(g15,g4) = 12.25
FEATURE [PartDesign::Pad] Pad
  Direction = (0,0,1)
  Length = 3.25
  Length2 = 10
  Profile = -> Sketch001
  ReferenceAxis = -> Sketch001 [N_Axis]
  Type = 0
  expr: Length = 3.25
FEATURE [PartDesign::CoordinateSystem] LCS_1
  AttacherType = Attacher::AttachEngine3D
  MapMode = 5
  Support = -> [XY_Plane]
FEATURE [Sketcher::SketchObject] Sketch002  label="TabSlotsBase"
  FullyConstrained = true
  MapMode = 5
  Support = -> [XY_Plane]
  expr: .Constraints.TRP = Sketch001.Constraints.TabRadialPos
  sketch-geometry (13):
    g0: LineSegment StartX=0 StartY=0 StartZ=0 EndX=-152 EndY=0 EndZ=0
    g1: LineSegment StartX=-152 StartY=0 StartZ=0 EndX=-152 EndY=28 EndZ=0
    g2: LineSegment StartX=-152 StartY=0 StartZ=0 EndX=-152 EndY=-28 EndZ=0
    g3: LineSegment StartX=-150.25 StartY=22.75 StartZ=0 EndX=-150.25 EndY=33.25 EndZ=0
    g4: LineSegment StartX=-150.25 StartY=33.25 StartZ=0 EndX=-153.75 EndY=33.25 EndZ=0
    g5: LineSegment StartX=-153.75 StartY=33.25 StartZ=0 EndX=-153.75 EndY=22.75 EndZ=0
    g6: LineSegment StartX=-153.75 StartY=22.75 StartZ=0 EndX=-150.25 EndY=22.75 EndZ=0
    g7: GeomPoint X=-152 Y=28 Z=0
    g8: LineSegment StartX=-150.25 StartY=-22.75 StartZ=0 EndX=-150.25 EndY=-33.25 EndZ=0
    g9: LineSegment StartX=-150.25 StartY=-33.25 StartZ=0 EndX=-153.75 EndY=-33.25 EndZ=0
    g10: LineSegment StartX=-153.75 StartY=-33.25 StartZ=0 EndX=-153.75 EndY=-22.75 EndZ=0
    g11: LineSegment StartX=-153.75 StartY=-22.75 StartZ=0 EndX=-150.25 EndY=-22.75 EndZ=0
    g12: GeomPoint X=-152 Y=-28 Z=0
  constraints (34):
    c: Coincident(g0,g-1)
    c: PointOnObject(g0,g-1)
    c: DistanceX(g0,g0) = 152  'TRP'
    c: Coincident(g1,g0)
    c: Vertical(g1)
    c: Coincident(g2,g0)
    c: Vertical(g2)
    c: DistanceY(g1,g1) = 28  'TabCntrOffset'
    c: Equal(g2,g1)
    c: Coincident(g3,g4)
    c: Coincident(g4,g5)
    c: Coincident(g5,g6)
    c: Coincident(g6,g3)
    c: Horizontal(g4)
    c: Horizontal(g6)
    c: Vertical(g3)
    c: Vertical(g5)
    c: Symmetric(g4,g3,g7)
    c: Coincident(g7,g1)
    c: Coincident(g8,g9)
    c: Coincident(g9,g10)
    c: Coincident(g10,g11)
    c: Coincident(g11,g8)
    c: Horizontal(g9)
    c: Horizontal(g11)
    c: Vertical(g8)
    c: Vertical(g10)
    c: Symmetric(g9,g8,g12)
    c: Coincident(g12,g2)
    c: Equal(g5,g10)
    c: Equal(g4,g11)
    c: DistanceY(g5,g5) = 10.5  'TabLength'
    c: DistanceX(g4,g4) = 3.5  'ThicknessClearance'
    c: DistanceY(g0,g3) = 22.75
FEATURE [PartDesign::Pocket] Pocket  label="TabSlotBase"
  BaseFeature = -> Pad
  Direction = (0,0,-1)
  Length = 5
  Length2 = 5
  Midplane = true
  Profile = -> Sketch002
  ReferenceAxis = -> Sketch002 [N_Axis]
  Type = 1
FEATURE [PartDesign::PolarPattern] PolarPattern  label="TabSlotPattern"
  Angle = 360
  Axis = -> Sketch002 [N_Axis]
  BaseFeature = -> Pocket
  Occurrences = 8
  Originals = -> [Pocket]
FEATURE [PartDesign::CoordinateSystem] LCS_Origin
  AttacherType = Attacher::AttachEngine3D
  MapMode = 2
  Support = -> [X_Axis001]
FEATURE [PartDesign::Plane] TXFP_SpacerSide
  Length = 100
  MapMode = 5
  Placement = pos=(0,0,0) rot=(1,0,0;3.14159rad)
  ResizeMode = 1
  Support = -> [PolarPattern]
  Width = 100
FEATURE [Sketcher::SketchObject] TabLCS
  FullyConstrained = true
  MapMode = 5
  Support = -> [XY_Plane]
  expr: .Constraints.TRP = Sketch002.Constraints.TRP
  expr: .Constraints.TabCntrOffset = Sketch002.Constraints.TabCntrOffset
  expr: .Constraints.TabLength = Sketch002.Constraints.TabLength
  expr: .Constraints.ThicknessClearance = Sketch002.Constraints.ThicknessClearance
  sketch-geometry (13):
    g0: LineSegment StartX=0 StartY=0 StartZ=0 EndX=-152 EndY=0 EndZ=0
    g1: LineSegment StartX=-152 StartY=0 StartZ=0 EndX=-152 EndY=28 EndZ=0
    g2: LineSegment StartX=-152 StartY=0 StartZ=0 EndX=-152 EndY=-28 EndZ=0
    g3: LineSegment StartX=-150.25 StartY=22.75 StartZ=0 EndX=-150.25 EndY=33.25 EndZ=0
    g4: LineSegment StartX=-150.25 StartY=33.25 StartZ=0 EndX=-153.75 EndY=33.25 EndZ=0
    g5: LineSegment StartX=-153.75 StartY=33.25 StartZ=0 EndX=-153.75 EndY=22.75 EndZ=0
    g6: LineSegment StartX=-153.75 StartY=22.75 StartZ=0 EndX=-150.25 EndY=22.75 EndZ=0
    g7: GeomPoint X=-152 Y=28 Z=0
    g8: LineSegment StartX=-150.25 StartY=-22.75 StartZ=0 EndX=-150.25 EndY=-33.25 EndZ=0
    g9: LineSegment StartX=-150.25 StartY=-33.25 StartZ=0 EndX=-153.75 EndY=-33.25 EndZ=0
    g10: LineSegment StartX=-153.75 StartY=-33.25 StartZ=0 EndX=-153.75 EndY=-22.75 EndZ=0
    g11: LineSegment StartX=-153.75 StartY=-22.75 StartZ=0 EndX=-150.25 EndY=-22.75 EndZ=0
    g12: GeomPoint X=-152 Y=-28 Z=0
  constraints (33):
    c: Coincident(g0,g-1)
    c: PointOnObject(g0,g-1)
    c: DistanceX(g0,g0) = 152  'TRP'
    c: Coincident(g1,g0)
    c: Vertical(g1)
    c: Coincident(g2,g0)
    c: Vertical(g2)
    c: DistanceY(g1,g1) = 28  'TabCntrOffset'
    c: Equal(g2,g1)
    c: Coincident(g3,g4)
    c: Coincident(g4,g5)
    c: Coincident(g5,g6)
    c: Coincident(g6,g3)
    c: Horizontal(g4)
    c: Horizontal(g6)
    c: Vertical(g3)
    c: Vertical(g5)
    c: Symmetric(g4,g3,g7)
    c: Coincident(g7,g1)
    c: Coincident(g8,g9)
    c: Coincident(g9,g10)
    c: Coincident(g10,g11)
    c: Coincident(g11,g8)
    c: Horizontal(g9)
    c: Horizontal(g11)
    c: Vertical(g8)
    c: Vertical(g10)
    c: Symmetric(g9,g8,g12)
    c: Coincident(g12,g2)
    c: Equal(g5,g10)
    c: Equal(g4,g11)
    c: DistanceY(g5,g5) = 10.5  'TabLength'
    c: DistanceX(g4,g4) = 3.5  'ThicknessClearance'
FEATURE [PartDesign::Line] TabSlotCL
  AttacherType = Attacher::AttachEngineLine
  Length = 200
  MapMode = 46
  Placement = pos=(-152,28,0) rot=(1,0,0;3.14159rad)
  ResizeMode = 1
  Support = -> [TabLCS,PolarPattern]
FEATURE [Sketcher::SketchObject] Sketch003
  FullyConstrained = true
  MapMode = 5
  Support = -> [XY_Plane]
  sketch-geometry (5):
    g0: LineSegment StartX=-175 StartY=-1.5 StartZ=0 EndX=-175 EndY=1.5 EndZ=0
    g1: LineSegment StartX=-175 StartY=1.5 StartZ=0 EndX=-185 EndY=1.5 EndZ=0
    g2: LineSegment StartX=-185 StartY=1.5 StartZ=0 EndX=-185 EndY=-1.5 EndZ=0
    g3: LineSegment StartX=-185 StartY=-1.5 StartZ=0 EndX=-175 EndY=-1.5 EndZ=0
    g4: GeomPoint X=-180 Y=0 Z=0
  constraints (13):
    c: Coincident(g0,g1)
    c: Coincident(g1,g2)
    c: Coincident(g2,g3)
    c: Coincident(g3,g0)
    c: Horizontal(g1)
    c: Horizontal(g3)
    c: Vertical(g0)
    c: Vertical(g2)
    c: Symmetric(g1,g0,g4)
    c: PointOnObject(g4,g-1)
    c: DistanceY(g2,g2) = 3
    c: DistanceX(g1,g1) = 10
    c: DistanceX(g2,g-1) = 185
FEATURE [PartDesign::Pocket] Pocket001
  BaseFeature = -> PolarPattern
  Direction = (0,0,-1)
  Length = 5
  Length2 = 5
  Midplane = true
  Profile = -> Sketch003
  ReferenceAxis = -> Sketch003 [N_Axis]
  Type = 1
FEATURE [PartDesign::PolarPattern] PolarPattern001
  Angle = 360
  Axis = -> Z_Axis
  BaseFeature = -> Pocket001
  Occurrences = 8
  Originals = -> [Pocket001]
FEATURE [Sketcher::SketchObject] Sketch004
  FullyConstrained = true
  MapMode = 5
  Support = -> [XY_Plane]
  sketch-geometry (10):
    g0: LineSegment StartX=-117.333 StartY=48.6008 StartZ=0 EndX=-117.333 EndY=-48.6008 EndZ=0
    g1: LineSegment StartX=-117.333 StartY=-48.6008 StartZ=0 EndX=-48.6008 EndY=-117.333 EndZ=0
    g2: LineSegment StartX=-48.6008 StartY=-117.333 StartZ=0 EndX=48.6008 EndY=-117.333 EndZ=0
    g3: LineSegment StartX=48.6008 StartY=-117.333 StartZ=0 EndX=117.333 EndY=-48.6008 EndZ=0
    g4: LineSegment StartX=117.333 StartY=-48.6008 StartZ=0 EndX=117.333 EndY=48.6008 EndZ=0
    g5: LineSegment StartX=117.333 StartY=48.6008 StartZ=0 EndX=48.6008 EndY=117.333 EndZ=0
    g6: LineSegment StartX=48.6008 StartY=117.333 StartZ=0 EndX=-48.6008 EndY=117.333 EndZ=0
    g7: LineSegment StartX=-48.6008 StartY=117.333 StartZ=0 EndX=-117.333 EndY=48.6008 EndZ=0
    g8: Circle CenterX=0 CenterY=0 CenterZ=0 NormalX=0 NormalY=0 NormalZ=1 AngleXU=0 Radius=127
    g9: Circle CenterX=-117.333 CenterY=48.6008 CenterZ=0 NormalX=0 NormalY=0 NormalZ=1 AngleXU=0 Radius=20
  constraints (22):
    c: Coincident(g0,g1)
    c: Coincident(g1,g2)
    c: Coincident(g2,g3)
    c: Coincident(g3,g4)
    c: Coincident(g4,g5)
    c: Coincident(g5,g6)
    c: Coincident(g6,g7)
    c: Coincident(g7,g0)
    c: Equal(g0, g1-g7) x7
    c: PointOnObject(g0,g8)
    c: PointOnObject(g1,g8)
    c: PointOnObject(g2,g8)
    c: PointOnObject(g3,g8)
    c: PointOnObject(g4,g8)
    c: PointOnObject(g5,g8)
    c: PointOnObject(g6,g8)
    c: PointOnObject(g7,g8)
    c: Coincident(g8,g-1)
    c: Diameter(g8) = 254
    c: Coincident(g9,g0)
    c: Vertical(g0)
    c: Diameter(g9) = 40
FEATURE [PartDesign::Pocket] Pocket002
  BaseFeature = -> PolarPattern001
  Direction = (0,0,-1)
  Length = 5
  Length2 = 5
  Midplane = true
  Profile = -> Sketch004
  ReferenceAxis = -> Sketch004 [N_Axis]
  Type = 1
FEATURE [PartDesign::PolarPattern] PolarPattern002
  Angle = 360
  Axis = -> Z_Axis
  BaseFeature = -> Pocket002
  Occurrences = 8
  Originals = -> [Pocket002]
FEATURE [PartDesign::Body] Body  label="TX_Faceplate"
  Group = -> [Sketch,Sketch001,Pad,LCS_1,Sketch002,Pocket,PolarPattern,TabLCS,Sketch003,Pocket001,PolarPattern001,Sketch004,Pocket002,PolarPattern002]
  Origin = -> Origin
  Tip = -> PolarPattern002
FEATURE [App::Part] TXFP
  Group = -> [LCS_Origin,Body,TXFP_SpacerSide,TabSlotCL]
  Origin = -> Origin001
---- part SpacerFlange_v2.FCStd = doc fcstd_1ae24769599b ----
FCSTD DOCUMENT  (FreeCAD 0.21R33771 (Git))
Label: SpacerFlange_v2
License: Creative Commons Attribution-ShareAlike 4.0
LicenseURL: https://creativecommons.org/licenses/by-sa/4.0/
objects: Sketcher::SketchObject×4, PartDesign::Point×1, PartDesign::Pad×1, PartDesign::Pocket×1, PartDesign::Mirrored×1, PartDesign::CoordinateSystem×1, PartDesign::Body×1, PartDesign::Line×1, App::Part×1
note: 13 computed .brp shape members not serialized (recipe doc carries the construction recipe); baked Part::Feature solids carry a one-line shape summary decoded from their .brp

FEATURE [Sketcher::SketchObject] Sketch  label="FlangeDims"
  FullyConstrained = false
  MapMode = 5
  Placement = pos=(0,0,0) rot=(1,0,0;1.5708rad)
  Support = -> [XZ_Plane]
  expr: Constraints[1] = 10 in
  expr: Constraints[53] = 16 in
  sketch-geometry (23):
    g0: Circle CenterX=0 CenterY=0 CenterZ=0 NormalX=0 NormalY=0 NormalZ=1 AngleXU=0 Radius=127
    g1: LineSegment StartX=-136.262 StartY=-56.4416 StartZ=0 EndX=-136.262 EndY=56.4416 EndZ=0
    g2: LineSegment StartX=-136.262 StartY=56.4416 StartZ=0 EndX=-139.262 EndY=56.4416 EndZ=0
    g3: LineSegment StartX=-139.262 StartY=56.4416 StartZ=0 EndX=-139.262 EndY=-56.4416 EndZ=0
    g4: LineSegment StartX=-139.262 StartY=-56.4416 StartZ=0 EndX=-136.262 EndY=-56.4416 EndZ=0
    g5: GeomPoint X=-137.762 Y=0 Z=0
    g6: LineSegment StartX=0 StartY=0 StartZ=0 EndX=-136.262 EndY=56.4416 EndZ=0
    g7: LineSegment StartX=-136.262 StartY=56.4416 StartZ=0 EndX=-136.262 EndY=-56.4416 EndZ=0
    g8: LineSegment StartX=-136.262 StartY=-56.4416 StartZ=0 EndX=-56.4416 EndY=-136.262 EndZ=0
    g9: LineSegment StartX=-56.4416 StartY=-136.262 StartZ=0 EndX=56.4416 EndY=-136.262 EndZ=0
    g10: LineSegment StartX=56.4416 StartY=-136.262 StartZ=0 EndX=136.262 EndY=-56.4416 EndZ=0
    g11: LineSegment StartX=136.262 StartY=-56.4416 StartZ=0 EndX=136.262 EndY=56.4416 EndZ=0
    g12: LineSegment StartX=136.262 StartY=56.4416 StartZ=0 EndX=56.4416 EndY=136.262 EndZ=0
    g13: LineSegment StartX=56.4416 StartY=136.262 StartZ=0 EndX=-56.4416 EndY=136.262 EndZ=0
    g14: LineSegment StartX=-56.4416 StartY=136.262 StartZ=0 EndX=-136.262 EndY=56.4416 EndZ=0
    g15: Circle CenterX=0 CenterY=0 CenterZ=0 NormalX=0 NormalY=0 NormalZ=1 AngleXU=0 Radius=147.489
    g16: Circle CenterX=0 CenterY=0 CenterZ=0 NormalX=0 NormalY=0 NormalZ=1 AngleXU=0 Radius=150.265
    g17: LineSegment StartX=-137.762 StartY=0 StartZ=0 EndX=-136.262 EndY=0 EndZ=0
    g18: LineSegment StartX=-131.631 StartY=0 StartZ=0 EndX=-127 EndY=0 EndZ=0
    g19: LineSegment StartX=-131.631 StartY=0 StartZ=0 EndX=-136.262 EndY=0 EndZ=0
    g20: Circle CenterX=0 CenterY=0 CenterZ=0 NormalX=0 NormalY=0 NormalZ=1 AngleXU=0 Radius=203.2
    g21: Circle CenterX=-117.333 CenterY=48.6008 CenterZ=0 NormalX=0 NormalY=0 NormalZ=1 AngleXU=0 Radius=15
    g22: LineSegment StartX=-139.262 StartY=34.4278 StartZ=0 EndX=-122.245 EndY=34.4278 EndZ=0
  constraints (60):
    c: Coincident(g0,g-1)
    c: Diameter(g0) = 254
    c: Coincident(g1,g2)
    c: Coincident(g2,g3)
    c: Coincident(g3,g4)
    c: Coincident(g4,g1)
    c: Horizontal(g2)
    c: Horizontal(g4)
    c: Vertical(g1)
    c: Vertical(g3)
    c: Symmetric(g2,g1,g5)
    c: PointOnObject(g5,g-1)
    c: Coincident(g6,g0)
    c: Coincident(g6,g1)
    c: DistanceX(g2,g2) = 3
    c: Coincident(g7,g8)
    c: Coincident(g8,g9)
    c: Coincident(g9,g10)
    c: Coincident(g10,g11)
    c: Coincident(g11,g12)
    c: Coincident(g12,g13)
    c: Coincident(g13,g14)
    c: Coincident(g14,g7)
    c: Equal(g7, g8-g14) x7
    c: PointOnObject(g7,g15)
    c: PointOnObject(g8,g15)
    c: PointOnObject(g9,g15)
    c: PointOnObject(g10,g15)
    c: PointOnObject(g11,g15)
    c: PointOnObject(g12,g15)
    c: PointOnObject(g13,g15)
    c: PointOnObject(g14,g15)
    c: Coincident(g15,g0)
    c: Coincident(g7,g1)
    c: Vertical(g7)
    c: Coincident(g16,g0)
    c: PointOnObject(g2,g16)
    c: Coincident(g17,g5)
    c: Horizontal(g17)
    c: Distance(g3) = 112.883
    c: Diameter(g15) = 294.978
    c: PointOnObject(g17,g1)
    c: PointOnObject(g18,g0)
    c: Horizontal(g18)
    c: Horizontal(g19)
    c: Diameter(g16) = 300.53
    c: Coincident(g20,g0)
    c: Diameter(g20) = 406.4
    c: PointOnObject(g21,g6)
    c: PointOnObject(g21,g0)
    c: Diameter(g21) = 30
    c: Equal(g19,g18)
    c: Coincident(g19,g17)
    c: Coincident(g19,g18)
    c: PointOnObject(g22,g3)
    c: Horizontal(g22)
    c: PointOnObject(g22,g21)
    c: PointOnObject(g22,g0)
    c: DistanceY(g0,g22) = 34.4278  'Max_Flange_Half'
    c: DistanceY(g0,g1) = 56.4416
FEATURE [PartDesign::Point] DatumPoint
  AttacherType = Attacher::AttachEnginePoint
  MapMode = 37
  Placement = pos=(-122.245,-7.6e-15,34.4278) rot=(0,0,1;0rad)
  Support = -> [Sketch]
FEATURE [Sketcher::SketchObject] Sketch001
  FullyConstrained = true
  MapMode = 5
  Placement = pos=(0,0,0) rot=(1,0,0;1.5708rad)
  Support = -> [XZ_Plane]
  sketch-geometry (25):
    g0: LineSegment StartX=38 StartY=-56 StartZ=0 EndX=38 EndY=56 EndZ=0
    g1: LineSegment StartX=38 StartY=56 StartZ=0 EndX=-38 EndY=56 EndZ=0
    g2: LineSegment StartX=-38 StartY=56 StartZ=0 EndX=-38 EndY=-56 EndZ=0
    g3: LineSegment StartX=-38 StartY=-56 StartZ=0 EndX=38 EndY=-56 EndZ=0
    g4: GeomPoint X=0 Y=0 Z=0
    g5: LineSegment StartX=-38 StartY=-23 StartZ=0 EndX=-41 EndY=-23 EndZ=0
    g6: LineSegment StartX=-41 StartY=-23 StartZ=0 EndX=-41 EndY=-33 EndZ=0
    g7: LineSegment StartX=-41 StartY=-33 StartZ=0 EndX=-38 EndY=-33 EndZ=0
    g8: LineSegment StartX=-38 StartY=23 StartZ=0 EndX=-41 EndY=23 EndZ=0
    g9: LineSegment StartX=-41 StartY=23 StartZ=0 EndX=-41 EndY=33 EndZ=0
    g10: LineSegment StartX=-41 StartY=33 StartZ=0 EndX=-38 EndY=33 EndZ=0
    g11: LineSegment StartX=38 StartY=33 StartZ=0 EndX=41 EndY=33 EndZ=0
    g12: LineSegment StartX=41 StartY=33 StartZ=0 EndX=41 EndY=23 EndZ=0
    g13: LineSegment StartX=41 StartY=23 StartZ=0 EndX=38 EndY=23 EndZ=0
    g14: LineSegment StartX=38 StartY=-23 StartZ=0 EndX=41 EndY=-23 EndZ=0
    g15: LineSegment StartX=41 StartY=-23 StartZ=0 EndX=41 EndY=-33 EndZ=0
    g16: LineSegment StartX=41 StartY=-33 StartZ=0 EndX=38 EndY=-33 EndZ=0
    g17: LineSegment StartX=-38 StartY=23 StartZ=0 EndX=-38 EndY=0 EndZ=0
    g18: LineSegment StartX=-38 StartY=0 StartZ=0 EndX=-38 EndY=-23 EndZ=0
    g19: LineSegment StartX=-38 StartY=-33 StartZ=0 EndX=-38 EndY=-56 EndZ=0
    g20: LineSegment StartX=-38 StartY=33 StartZ=0 EndX=-38 EndY=56 EndZ=0
    g21: LineSegment StartX=38 StartY=56 StartZ=0 EndX=38 EndY=33 EndZ=0
    g22: LineSegment StartX=38 StartY=23 StartZ=0 EndX=38 EndY=0 EndZ=0
    g23: LineSegment StartX=38 StartY=0 StartZ=0 EndX=38 EndY=-23 EndZ=0
    g24: LineSegment StartX=38 StartY=-33 StartZ=0 EndX=38 EndY=-56 EndZ=0
  constraints (71):
    c: Coincident(g0,g1)
    c: Coincident(g1,g2)
    c: Coincident(g2,g3)
    c: Coincident(g3,g0)
    c: Horizontal(g1)
    c: Horizontal(g3)
    c: Vertical(g0)
    c: Vertical(g2)
    c: Symmetric(g1,g0,g4)
    c: Coincident(g4,g-1)
    c: DistanceY(g4,g0) = 56
    c: DistanceX(g4,g0) = 38
    c: PointOnObject(g5,g2)
    c: Horizontal(g5)
    c: Coincident(g6,g5)
    c: Vertical(g6)
    c: Coincident(g7,g6)
    c: PointOnObject(g7,g2)
    c: Horizontal(g7)
    c: PointOnObject(g8,g2)
    c: Coincident(g9,g8)
    c: Vertical(g9)
    c: Coincident(g10,g9)
    c: PointOnObject(g10,g2)
    c: Horizontal(g10)
    c: PointOnObject(g11,g0)
    c: Horizontal(g11)
    c: Coincident(g12,g11)
    c: Vertical(g12)
    c: Coincident(g13,g12)
    c: PointOnObject(g13,g0)
    c: Horizontal(g13)
    c: PointOnObject(g14,g0)
    c: Horizontal(g14)
    c: Vertical(g15)
    c: Coincident(g16,g15)
    c: PointOnObject(g16,g0)
    c: Horizontal(g16)
    c: Horizontal(g8)
    c: DistanceY(g9,g9) = 10
    c: Equal(g9,g12)
    c: Equal(g12,g15)
    c: Equal(g15,g6)
    c: DistanceX(g10,g10) = 3
    c: Equal(g10,g11)
    c: Equal(g11,g14)
    c: Equal(g14,g5)
    c: Coincident(g17,g8)
    c: PointOnObject(g17,g-1)
    c: Coincident(g18,g17)
    c: Coincident(g18,g5)
    c: PointOnObject(g17,g2)
    c: Coincident(g19,g7)
    c: Coincident(g19,g3)
    c: Coincident(g20,g10)
    c: Coincident(g20,g1)
    c: Coincident(g21,g1)
    c: Coincident(g21,g11)
    c: Coincident(g22,g13)
    c: PointOnObject(g22,g-1)
    c: Coincident(g23,g22)
    c: Coincident(g23,g14)
    c: Coincident(g24,g16)
    c: Coincident(g24,g3)
    c: PointOnObject(g22,g0)
    c: Equal(g17,g18)
    c: Equal(g17,g22)
    c: Equal(g22,g23)
    c: Equal(g20,g17)
    c: Coincident(g15,g14)
    c: DistanceY(g22,g12) = 23
FEATURE [PartDesign::Pad] Pad
  Direction = (0,-1,-2e-16)
  Length = 3
  Length2 = 10
  Midplane = true
  Placement = pos=(0,0,0) rot=(1,0,0;1.5708rad)
  Profile = -> Sketch001
  ReferenceAxis = -> Sketch001 [N_Axis]
  Type = 0
FEATURE [Sketcher::SketchObject] Sketch002
  FullyConstrained = true
  MapMode = 5
  Placement = pos=(0,0,0) rot=(1,0,0;1.5708rad)
  Support = -> [XZ_Plane]
  sketch-geometry (6):
    g0: LineSegment StartX=25.25 StartY=-1.75 StartZ=0 EndX=25.25 EndY=1.75 EndZ=0
    g1: LineSegment StartX=25.25 StartY=1.75 StartZ=0 EndX=14.75 EndY=1.75 EndZ=0
    g2: LineSegment StartX=14.75 StartY=1.75 StartZ=0 EndX=14.75 EndY=-1.75 EndZ=0
    g3: LineSegment StartX=14.75 StartY=-1.75 StartZ=0 EndX=25.25 EndY=-1.75 EndZ=0
    g4: GeomPoint X=20 Y=0 Z=0
    g5: LineSegment StartX=38 StartY=10 StartZ=0 EndX=38 EndY=0 EndZ=0
  constraints (18):
    c: Coincident(g0,g1)
    c: Coincident(g1,g2)
    c: Coincident(g2,g3)
    c: Coincident(g3,g0)
    c: Horizontal(g1)
    c: Horizontal(g3)
    c: Vertical(g0)
    c: Vertical(g2)
    c: Symmetric(g1,g0,g4)
    c: DistanceY(g0,g0) = 3.5
    c: PointOnObject(g4,g-1)
    c: DistanceX(g1,g1) = 10.5
    c: DistanceX(g-1,g4) = 20
    c: Vertical(g5)
    c: PointOnObject(g5,g-1)
    c: DistanceX(g-1,g5) = 38
    c: DistanceY(g5,g5) = 10
    c: DistanceX(g0,g5) = 12.75
FEATURE [PartDesign::Pocket] Pocket  label="VerticalGussetSlot"
  BaseFeature = -> Pad
  Direction = (0,1,2e-16)
  Length = 5
  Length2 = 5
  Midplane = true
  Placement = pos=(0,0,0) rot=(1,0,0;1.5708rad)
  Profile = -> Sketch002
  ReferenceAxis = -> Sketch002 [N_Axis]
  Type = 1
FEATURE [PartDesign::Mirrored] Mirrored
  BaseFeature = -> Pocket
  MirrorPlane = -> Sketch002 [V_Axis]
  Originals = -> [Pocket]
  Placement = pos=(0,0,0) rot=(1,0,0;1.5708rad)
FEATURE [PartDesign::CoordinateSystem] LCS_Origin
  AttacherType = Attacher::AttachEngine3D
  MapMode = 2
  Support = -> [X_Axis001]
FEATURE [Sketcher::SketchObject] Sketch_1
  FullyConstrained = true
  MapMode = 5
  Placement = pos=(0,0,0) rot=(0.57735,0.57735,0.57735;2.0944rad)
  Support = -> [YZ_Plane]
  sketch-geometry (2):
    g0: LineSegment StartX=0 StartY=0 StartZ=0 EndX=0 EndY=17 EndZ=0
    g1: GeomPoint X=0 Y=12 Z=0
  constraints (5):
    c: PointOnObject(g1,g0)
    c: Distance(g-1,g1) = 12
    c: Distance(g1,g0) = 5
    c: Coincident(g0,g-1)
    c: PointOnObject(g0,g-2)
FEATURE [PartDesign::Body] Body
  Group = -> [Sketch,DatumPoint,Sketch001,Pad,Sketch002,Pocket,Mirrored,Sketch_1]
  Origin = -> Origin
  Tip = -> Mirrored
FEATURE [PartDesign::Line] TabCenterAxis
  AttacherType = Attacher::AttachEngineLine
  Length = 200
  MapMode = 46
  Placement = pos=(-3.8e-15,3.8e-15,17) rot=(0,1,0;1.5708rad)
  ResizeMode = 1
  Support = -> [Sketch_1,YZ_Plane]
FEATURE [App::Part] TabFlange
  Group = -> [LCS_Origin,Body,TabCenterAxis]
  Origin = -> Origin001
